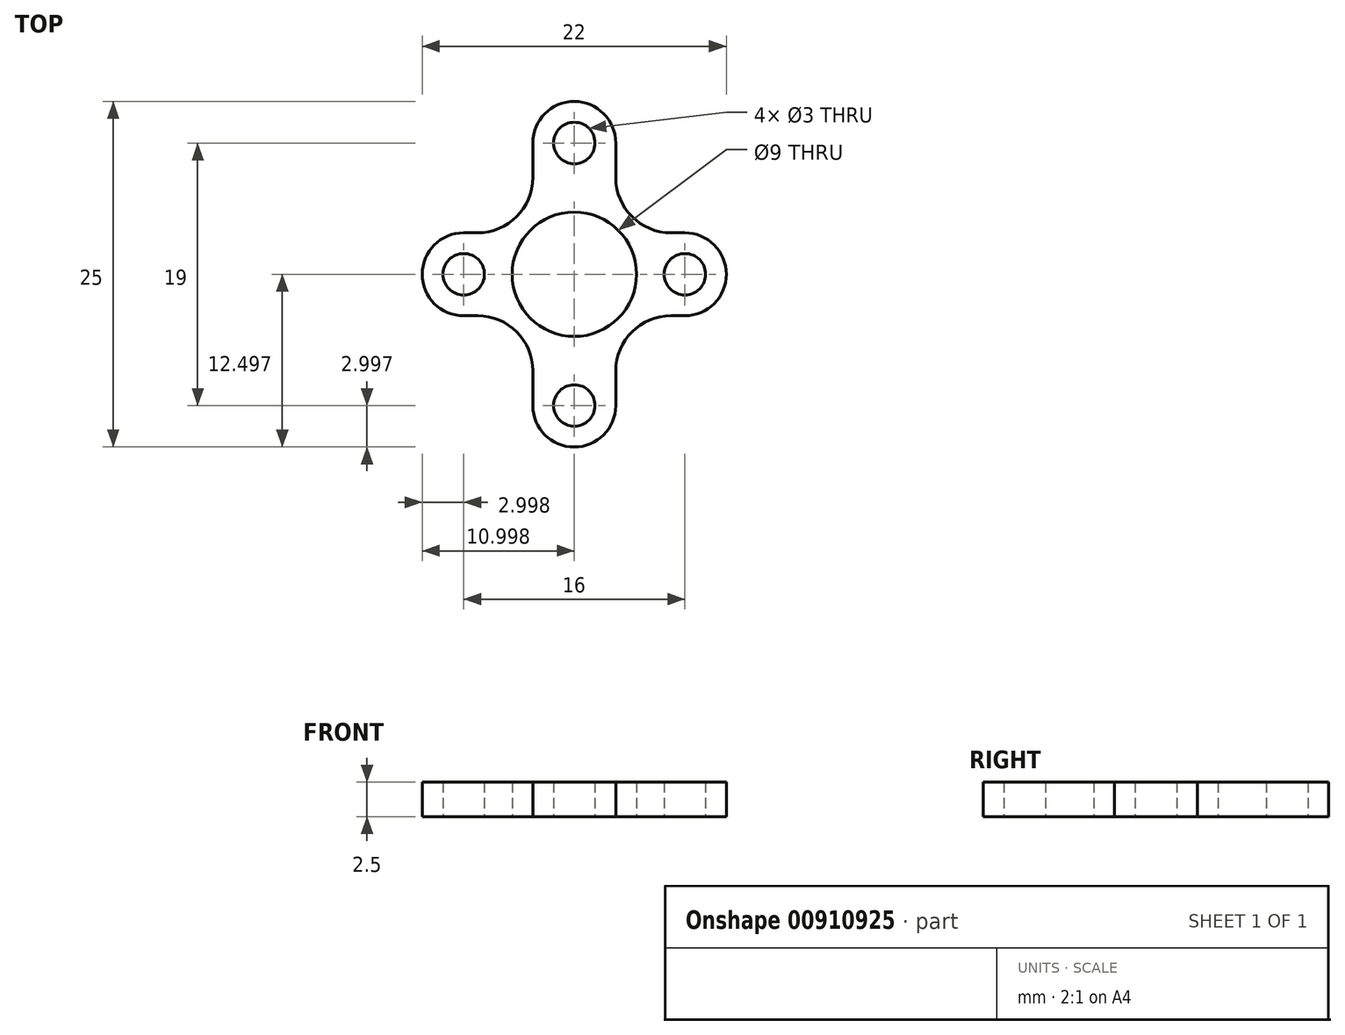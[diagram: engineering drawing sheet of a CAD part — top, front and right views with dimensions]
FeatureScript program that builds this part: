
annotation { "Feature Type Name" : "Feature", "Feature Type Description" : "" }
export const myFeature = defineFeature(function(context is Context, id is Id, definition is map)
    precondition{}
    {
        {
            var Q0;
            Q0=qCreatedBy(makeId("Top.planeOp"),FACE);
            var sketch = newSketch(context, id + "F0", { "sketchPlane" : qUnion([Q0])});
            skCircle(sketch, "E0", {"center": v(-0.33, -0.01) * mm, "radius": 8 * mm, "construction": true});
            skCircle(sketch, "E1", {"center": v(-0.33, 9.49) * mm, "radius": 1.5 * mm});
            skCircle(sketch, "E2", {"center": v(-8.33, -0.01) * mm, "radius": 1.5 * mm});
            skCircle(sketch, "E3", {"center": v(7.67, -0.01) * mm, "radius": 1.5 * mm});
            skCircle(sketch, "E4", {"center": v(-0.33, -9.51) * mm, "radius": 1.5 * mm});
            skCircle(sketch, "E5", {"center": v(-0.33, -0.01) * mm, "radius": 5.5 * mm, "construction": true});
            skLineSegment(sketch, "E6", {"start": v(-13.05, 12.7) * mm, "end": v(-0.33, -0.01) * mm, "construction": true});
            skLineSegment(sketch, "E7", {"start": v(-0.33, -0.01) * mm, "end": v(13.46, -13.8) * mm, "construction": true});
            skLineSegment(sketch, "E8", {"start": v(12.42, 12.74) * mm, "end": v(-0.33, -0.01) * mm, "construction": true});
            skLineSegment(sketch, "E9", {"start": v(-0.33, -0.01) * mm, "end": v(-11.08, -10.76) * mm, "construction": true});
            skLineSegment(sketch, "E10", {"start": v(-0.33, -0.01) * mm, "end": v(19.86, -0.01) * mm, "construction": true});
            skCircle(sketch, "E11", {"center": v(-0.33, 9.49) * mm, "radius": 3 * mm, "construction": true});
            skCircle(sketch, "E12", {"center": v(-8.33, -0.01) * mm, "radius": 3 * mm, "construction": true});
            skCircle(sketch, "E13", {"center": v(-0.33, -9.51) * mm, "radius": 3 * mm, "construction": true});
            skCircle(sketch, "E14", {"center": v(7.67, -0.01) * mm, "radius": 3 * mm, "construction": true});
            skLineSegment(sketch, "E15", {"start": v(-8.33, -3.01) * mm, "end": v(-7.33, -3.01) * mm});
            skLineSegment(sketch, "E16", {"start": v(-3.33, -7.01) * mm, "end": v(-3.33, -9.51) * mm});
            skLineSegment(sketch, "E17", {"start": v(2.67, -9.51) * mm, "end": v(2.67, -7.01) * mm});
            skLineSegment(sketch, "E18", {"start": v(6.67, -3.01) * mm, "end": v(7.67, -3.01) * mm});
            skLineSegment(sketch, "E19", {"start": v(7.67, 2.99) * mm, "end": v(6.67, 2.99) * mm});
            skLineSegment(sketch, "E20", {"start": v(2.67, 6.99) * mm, "end": v(2.67, 9.49) * mm});
            skLineSegment(sketch, "E21", {"start": v(-3.33, 9.49) * mm, "end": v(-3.33, 6.99) * mm});
            skLineSegment(sketch, "E22", {"start": v(-7.33, 2.99) * mm, "end": v(-8.33, 2.99) * mm});
            skArc(sketch, "E23", {"start": v(-8.33, -3.01) * mm, "mid": v(-11.33, -0.01) * mm, "end": v(-8.33, 2.99) * mm});
            skArc(sketch, "E24", {"start": v(-3.33, 9.49) * mm, "mid": v(-0.33, 12.49) * mm, "end": v(2.67, 9.49) * mm});
            skArc(sketch, "E25", {"start": v(7.67, 2.99) * mm, "mid": v(10.67, -0.01) * mm, "end": v(7.67, -3.01) * mm});
            skArc(sketch, "E26", {"start": v(2.67, -9.51) * mm, "mid": v(-0.33, -12.51) * mm, "end": v(-3.33, -9.51) * mm});
            skPoint(sketch, "E27.visualSharp", {"position": v(-3.33, 2.99) * mm});
            skArc(sketch, "E27.filletArc", {"start": v(-7.33, 2.99) * mm, "mid": v(-4.5, 4.16) * mm, "end": v(-3.33, 6.99) * mm});
            skPoint(sketch, "E28.visualSharp", {"position": v(2.67, 2.99) * mm});
            skArc(sketch, "E28.filletArc", {"start": v(2.67, 6.99) * mm, "mid": v(3.84, 4.16) * mm, "end": v(6.67, 2.99) * mm});
            skPoint(sketch, "E29.visualSharp", {"position": v(2.67, -3.01) * mm});
            skArc(sketch, "E29.filletArc", {"start": v(6.67, -3.01) * mm, "mid": v(3.84, -4.18) * mm, "end": v(2.67, -7.01) * mm});
            skPoint(sketch, "E30.visualSharp", {"position": v(-3.33, -3.01) * mm});
            skArc(sketch, "E30.filletArc", {"start": v(-3.33, -7.01) * mm, "mid": v(-4.5, -4.18) * mm, "end": v(-7.33, -3.01) * mm});
            skCircle(sketch, "E31", {"center": v(-0.33, -0.01) * mm, "radius": 4.5 * mm});
            skCircle(sketch, "E32", {"center": v(-0.33, -0.01) * mm, "radius": 9.5 * mm, "construction": true});
            skSolve(sketch);
        }
        {
            var Q0;
            Q0=qSketchRegion(id+"F0",true);
            extrude(context, id + "F1", {"entities" : qUnion([Q0]), "depth" : 2.5 * mm, "offsetDistance" : 25.4 * mm});
        }
    });
